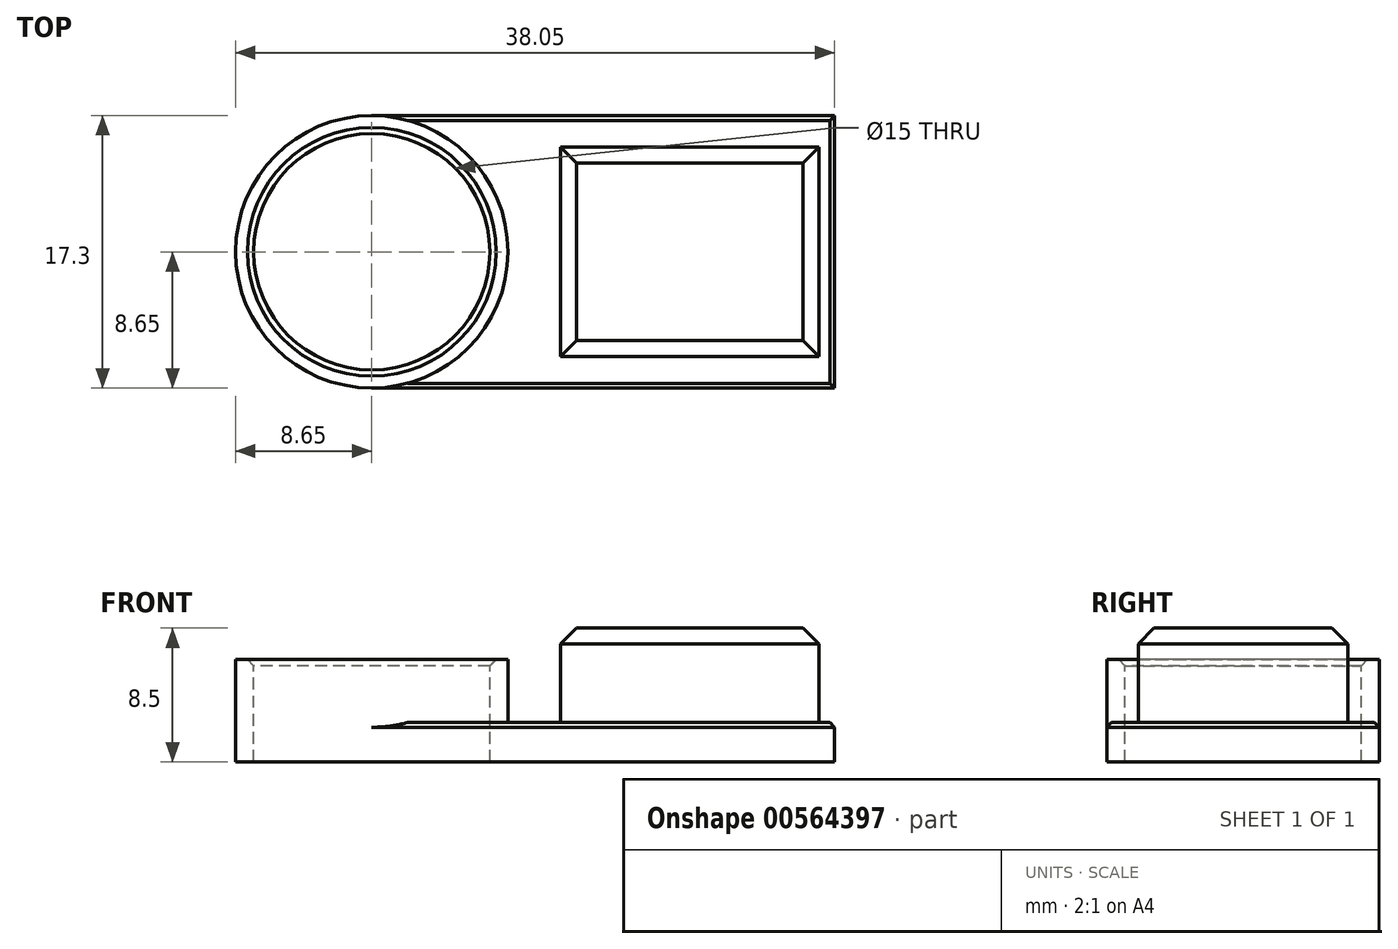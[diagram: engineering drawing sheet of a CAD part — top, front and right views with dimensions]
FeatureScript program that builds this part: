
annotation { "Feature Type Name" : "Feature", "Feature Type Description" : "" }
export const myFeature = defineFeature(function(context is Context, id is Id, definition is map)
    precondition{}
    {
        {
            var Q0;
            Q0=qCreatedBy(makeId("Top.planeOp"),FACE);
            var sketch = newSketch(context, id + "F0", { "sketchPlane" : qUnion([Q0])});
            skLineSegment(sketch, "E0.bottom", {"start": v(0, 0) * mm, "end": v(-29.4, 0) * mm});
            skLineSegment(sketch, "E0.top", {"start": v(0, 17.3) * mm, "end": v(-29.4, 17.3) * mm});
            skLineSegment(sketch, "E0.left", {"start": v(0, 0) * mm, "end": v(0, 17.3) * mm});
            skLineSegment(sketch, "E1.bottom", {"start": v(-1, 2) * mm, "end": v(-17.4, 2) * mm});
            skLineSegment(sketch, "E1.top", {"start": v(-1, 15.3) * mm, "end": v(-17.4, 15.3) * mm});
            skLineSegment(sketch, "E1.left", {"start": v(-1, 2) * mm, "end": v(-1, 15.3) * mm});
            skLineSegment(sketch, "E1.right", {"start": v(-17.4, 2) * mm, "end": v(-17.4, 15.3) * mm});
            skCircle(sketch, "E2", {"center": v(-29.4, 8.65) * mm, "radius": 7.5 * mm});
            skPoint(sketch, "E3", {"position": v(-17.4, 8.65) * mm});
            skPoint(sketch, "E4.visualSharp", {"position": v(-37.3, 17.3) * mm});
            skPoint(sketch, "E5.visualSharp", {"position": v(-37.3, 0) * mm});
            skCircle(sketch, "E6", {"center": v(-29.4, 8.65) * mm, "radius": 8.65 * mm});
            skSolve(sketch);
        }
        {
            var Q0;
            {var subQ1=sQuery(id+"F0.wireOp",EDGE,"E0.bottom");Q0=makeQuery(id+"F0.imprint","IMPRINT",FACE,{"disambiguationData":[TD([[makeQuery(id+"F0.imprint","IMPRINT",EDGE,{"derivedFrom":subQ1}),-1.0]])]});}
            var Q1;
            Q1=makeQuery(id+"F0.imprint","IMPRINT",FACE,{"disambiguationData":[TD([[makeQuery(id+"F0.imprint","IMPRINT",EDGE,{"derivedFrom":sQuery(id+"F0.wireOp",EDGE,"E1.bottom")}),-1.0]])]});
            var Q2;
            Q2=makeQuery(id+"F0.imprint","IMPRINT",FACE,{"disambiguationData":[TD([[makeQuery(id+"F0.imprint","IMPRINT",EDGE,{"derivedFrom":sQuery(id+"F0.wireOp",EDGE,"E2")}),-1.0]])]});
            extrude(context, id + "F1", {"entities" : qUnion([Q0, Q1, Q2]), "oppositeDirection" : true, "depth" : 2.5 * mm, "offsetDistance" : 25 * mm});
        }
        {
            var Q0;
            Q0=makeQuery(id+"F0.imprint","IMPRINT",FACE,{"disambiguationData":[TD([[makeQuery(id+"F0.imprint","IMPRINT",EDGE,{"derivedFrom":sQuery(id+"F0.wireOp",EDGE,"E1.bottom")}),-1.0]])]});
            extrude(context, id + "F2", {"entities" : qUnion([Q0]), "operationType" : NewBodyOperationType.ADD, "depth" : 6 * mm, "offsetDistance" : 25 * mm});
        }
        {
            var Q0;
            Q0=makeQuery(id+"F2.opExtrude","CAP_FACE",FACE,{"disambiguationData":[OSD([sQuery(id+"F0.wireOp",EDGE,"E1.bottom"),sQuery(id+"F0.wireOp",EDGE,"E1.top"),sQuery(id+"F0.wireOp",EDGE,"E1.left"),sQuery(id+"F0.wireOp",EDGE,"E1.right")])],"isStart":false});
            chamfer(context, id + "F3", {"entities" : qUnion([Q0]), "width" : 1 * mm, "tangentPropagation" : true});
        }
        {
            var Q0;
            Q0=makeQuery(id+"F0.imprint","IMPRINT",FACE,{"disambiguationData":[TD([[makeQuery(id+"F0.imprint","IMPRINT",EDGE,{"derivedFrom":sQuery(id+"F0.wireOp",EDGE,"E2")}),-1.0]])]});
            extrude(context, id + "F4", {"entities" : qUnion([Q0]), "operationType" : NewBodyOperationType.ADD, "depth" : 4 * mm, "offsetDistance" : 25 * mm});
        }
        {
            var Q0;
            Q0=makeQuery(id+"F4.opExtrude","CAP_EDGE",EDGE,{"disambiguationData":[OSD([sQuery(id+"F0.wireOp",EDGE,"E2")])],"isStart":false});
            chamfer(context, id + "F5", {"entities" : qUnion([Q0]), "width" : 0.4 * mm, "tangentPropagation" : true});
        }
        {
            var Q0;
            Q0=makeQuery(id+"F1.opExtrude","CAP_EDGE",EDGE,{"disambiguationData":[OSD([sQuery(id+"F0.wireOp",EDGE,"E0.bottom")])],"isStart":true});
            var Q1;
            Q1=makeQuery(id+"F1.opExtrude","CAP_EDGE",EDGE,{"disambiguationData":[OSD([sQuery(id+"F0.wireOp",EDGE,"E0.top")])],"isStart":true});
            var Q2;
            Q2=makeQuery(id+"F1.opExtrude","CAP_EDGE",EDGE,{"disambiguationData":[OSD([sQuery(id+"F0.wireOp",EDGE,"E0.left")])],"isStart":true});
            chamfer(context, id + "F6", {"entities" : qUnion([Q0, Q1, Q2]), "width" : 0.3 * mm, "tangentPropagation" : true});
        }
    });
